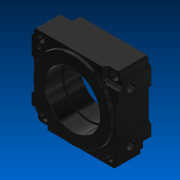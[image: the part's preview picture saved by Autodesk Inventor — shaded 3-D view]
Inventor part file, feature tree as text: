
AUTODESK INVENTOR PART (.ipt)
format: ipt  version: 2022.2 (Build 262287000, 287)  size: 262,656 bytes
history: native  units: in
note: dims shown in document units (in); Inventor stores cm internally (conversion verified against a paired STEP export)
features: chamfer x1
ambient origin geometry x8: Origin, YZ Plane, XZ Plane, XY Plane, X Axis, Y Axis, Z Axis, Center Point
bodies: Solid1 (feature_tree)
feature tree (1):
  chamfer  "Chamfer2"  [1 undecoded]
note: 1 required parameter value undecoded (feature->parameter linkage not recoverable at this tier; creation-order binding heuristic only, values carry confidence <= 0.55)
